# Revit family: Casement_34_E_Side_Hung_Standard
name_source: partatom
category: Windows
revit_build: Autodesk Revit 2014 (Build: 20130308_1515(x64)
units: mm (PartAtom-declared; Revit-internal decimal feet)

## types (17) — shared parameters
Aluminium Thickness = 1 mm  [stored 0.00328084 ft]
Area Pane Left Top = 0.52 m²
Bead SG Gap = 13 mm  [stored 0.0426509 ft]
Casement Dimension = 34 mm  [stored 0.111549 ft]
Custom Sash Height = 1154 mm  [stored 3.78609 ft]
Custom Sash Width = 554 mm  [stored 1.81759 ft]
DG Extrusion Start = 7 mm  [stored 0.0229659 ft]
DG Gasket Finish = Double Glazing Gasket Material
DG Thickness Calc = 4 mm  [stored 0.0131234 ft]
Default Sill Height = 800 mm  [stored 2.62467 ft]
Depth Bead = 20 mm  [stored 0.0656168 ft]
Description = Window 34mm, Type E side hung
Frame Center Offset = 17 mm
Height Panel 1 = 1139 mm  [stored 3.73688 ft]
Height Sash = 1124 mm  [stored 3.68766 ft]
Height Sash Opening = 1154 mm  [stored 3.78609 ft]
Length Transom = 540 mm  [stored 1.77165 ft]
Limit Fixed Pane Height Max = 1800 mm
Limit Fixed Pane Height Min = 200 mm  [stored 0.656168 ft]
Limit Fixed Pane Width Max = 1500 mm  [stored 4.92126 ft]
Limit Fixed Pane Width Min = 200 mm  [stored 0.656168 ft]
Limit Sash Height Max = 1500 mm  [stored 4.92126 ft]
Limit Sash Height Min = 300 mm  [stored 0.984252 ft]
Limit Sash Width Max = 700 mm  [stored 2.29659 ft]
Limit Sash Width Min = 300 mm  [stored 0.984252 ft]
Limit Window Height Max = 1860 mm
Limit Window Height Min = 1430 mm  [stored 4.6916 ft]
Limit Window Width Max = 2130 mm
Limit Window Width Min = 830 mm  [stored 2.7231 ft]
Manufacturer = Crealco
Max System DG One Piece Thickness = 4 mm  [stored 0.0131234 ft]
Max System DG Unit Thickness = 20 mm  [stored 0.0656168 ft]
Model = Casement 34
Offset Bead SG Center Reversed = 17 mm
Offset Mullion Left = 570 mm  [stored 1.87008 ft]
Offset Panel 3 Bead Top = 1200 mm
Offset Panel 4 Left = 600 mm  [stored 1.9685 ft]
Offset Sash Left = 23 mm  [stored 0.0754593 ft]
Offset Sash Top = 23 mm  [stored 0.0754593 ft]
Offset Transom Top = 1170 mm
Offset Window Exterior = 17 mm
SG Gasket Thickness = 6 mm  [stored 0.019685 ft]
Sash Center Offset = 14 mm  [stored 0.0459318 ft]
Sash Overlap = 7 mm  [stored 0.0229659 ft]
Sash Spacing Inner = 8 mm  [stored 0.0262467 ft]
Wall Closure = By host
Width Bead = 15 mm  [stored 0.0492126 ft]
Width Fixed Pane Bottom LHS = 540 mm  [stored 1.77165 ft]
Width Panel 1 = 540 mm  [stored 1.77165 ft]
Width Profile = 30 mm  [stored 0.0984252 ft]
Width Sash = 524 mm  [stored 1.71916 ft]
Width Sash Opening = 554 mm  [stored 1.81759 ft]
zero-valued in all types: Window Exterior Offset

## per-type parameters (varying)
- 34-0915S-1000Pa: Area Pane Left Bottom=0.13 m²; Area Pane Right=0.36 m²; Clearvue Insulated LowE SHGC Value=0.517; Clearvue Insulated LowE U Value=4.01; Clearvue Insulated SHGC Value=0.586; Clearvue Insulated U Value=4.37; Clearvue SHGC Value=0.636; Custom Windload=1000 mm  [stored 3.28084 ft]; Custom Window Height=1490 mm  [stored 4.88845 ft]; Custom Window Width=890 mm  [stored 2.91995 ft]; Depth Mullion=54 mm  [stored 0.177165 ft]; Energy Advantage SHGC Value=0.571; Energy Advantage U Value=5.2; Height=1490 mm  [stored 4.88845 ft]; Height Fixed Pane Bottom LHS=260 mm  [stored 0.853018 ft]; Height Fixed Pane RHS=1430 mm  [stored 4.6916 ft]; Intruderprufe LowE SHGC Value=0.537; Intruderprufe LowE U Value=5.04; Intruderprufe SHGC Value=0.599; Intruderprufe U Value=6.35; Length Mullion=1490 mm  [stored 4.88845 ft]; Max Pane Area=0.52 m²; Mullion Depth Windload Based=54 mm  [stored 0.177165 ft]; Width=890 mm  [stored 2.91995 ft]; Width Fixed Pane RHS=260 mm  [stored 0.853018 ft]; Windload Design=1000 mm  [stored 3.28084 ft]
- 34-0915S-1500Pa: Area Pane Left Bottom=0.13 m²; Area Pane Right=0.36 m²; Clearvue Insulated LowE SHGC Value=0.517; Clearvue Insulated LowE U Value=4.01; Clearvue Insulated SHGC Value=0.586; Clearvue Insulated U Value=4.37; Clearvue SHGC Value=0.636; Custom Windload=1500 mm  [stored 4.92126 ft]; Custom Window Height=1490 mm  [stored 4.88845 ft]; Custom Window Width=890 mm  [stored 2.91995 ft]; Depth Mullion=54 mm  [stored 0.177165 ft]; Energy Advantage SHGC Value=0.571; Energy Advantage U Value=5.2; Height=1490 mm  [stored 4.88845 ft]; Height Fixed Pane Bottom LHS=260 mm  [stored 0.853018 ft]; Height Fixed Pane RHS=1430 mm  [stored 4.6916 ft]; Intruderprufe LowE SHGC Value=0.537; Intruderprufe LowE U Value=5.04; Intruderprufe SHGC Value=0.599; Intruderprufe U Value=6.35; Length Mullion=1490 mm  [stored 4.88845 ft]; Max Pane Area=0.52 m²; Mullion Depth Windload Based=54 mm  [stored 0.177165 ft]; Width=890 mm  [stored 2.91995 ft]; Width Fixed Pane RHS=260 mm  [stored 0.853018 ft]; Windload Design=1500 mm  [stored 4.92126 ft]
- 34-0915S-2000Pa: Area Pane Left Bottom=0.13 m²; Area Pane Right=0.36 m²; Clearvue Insulated LowE SHGC Value=0.517; Clearvue Insulated LowE U Value=4.01; Clearvue Insulated SHGC Value=0.586; Clearvue Insulated U Value=4.37; Clearvue SHGC Value=0.636; Custom Windload=2000 mm; Custom Window Height=1490 mm  [stored 4.88845 ft]; Custom Window Width=890 mm  [stored 2.91995 ft]; Depth Mullion=54 mm  [stored 0.177165 ft]; Energy Advantage SHGC Value=0.571; Energy Advantage U Value=5.2; Height=1490 mm  [stored 4.88845 ft]; Height Fixed Pane Bottom LHS=260 mm  [stored 0.853018 ft]; Height Fixed Pane RHS=1430 mm  [stored 4.6916 ft]; Intruderprufe LowE SHGC Value=0.537; Intruderprufe LowE U Value=5.04; Intruderprufe SHGC Value=0.599; Intruderprufe U Value=6.35; Length Mullion=1490 mm  [stored 4.88845 ft]; Max Pane Area=0.52 m²; Mullion Depth Windload Based=54 mm  [stored 0.177165 ft]; Width=890 mm  [stored 2.91995 ft]; Width Fixed Pane RHS=260 mm  [stored 0.853018 ft]; Windload Design=2000 mm
- 34-1515S-1000Pa: Area Pane Left Bottom=0.13 m²; Area Pane Right=1.21 m²; Clearvue Insulated LowE SHGC Value=0.621; Clearvue Insulated LowE U Value=3.57; Clearvue Insulated SHGC Value=0.694; Clearvue Insulated U Value=4.15; Clearvue SHGC Value=0.769; Custom Windload=1000 mm  [stored 3.28084 ft]; Custom Window Height=1490 mm  [stored 4.88845 ft]; Custom Window Width=1490 mm  [stored 4.88845 ft]; Depth Mullion=54 mm  [stored 0.177165 ft]; Energy Advantage SHGC Value=0.689; Energy Advantage U Value=5.08; Height=1490 mm  [stored 4.88845 ft]; Height Fixed Pane Bottom LHS=260 mm  [stored 0.853018 ft]; Height Fixed Pane RHS=1430 mm  [stored 4.6916 ft]; Intruderprufe LowE SHGC Value=0.644; Intruderprufe LowE U Value=4.9; Intruderprufe SHGC Value=0.726; Intruderprufe U Value=6.68; Length Mullion=1490 mm  [stored 4.88845 ft]; Max Pane Area=1.21 m²; Mullion Depth Windload Based=54 mm  [stored 0.177165 ft]; Width=1490 mm  [stored 4.88845 ft]; Width Fixed Pane RHS=860 mm  [stored 2.82152 ft]; Windload Design=1000 mm  [stored 3.28084 ft]
- 34-1515S-1500Pa: Area Pane Left Bottom=0.13 m²; Area Pane Right=1.21 m²; Clearvue Insulated LowE SHGC Value=0.621; Clearvue Insulated LowE U Value=3.57; Clearvue Insulated SHGC Value=0.694; Clearvue Insulated U Value=4.15; Clearvue SHGC Value=0.769; Custom Windload=1500 mm  [stored 4.92126 ft]; Custom Window Height=1490 mm  [stored 4.88845 ft]; Custom Window Width=1490 mm  [stored 4.88845 ft]; Depth Mullion=54 mm  [stored 0.177165 ft]; Energy Advantage SHGC Value=0.689; Energy Advantage U Value=5.08; Height=1490 mm  [stored 4.88845 ft]; Height Fixed Pane Bottom LHS=260 mm  [stored 0.853018 ft]; Height Fixed Pane RHS=1430 mm  [stored 4.6916 ft]; Intruderprufe LowE SHGC Value=0.644; Intruderprufe LowE U Value=4.9; Intruderprufe SHGC Value=0.726; Intruderprufe U Value=6.68; Length Mullion=1490 mm  [stored 4.88845 ft]; Max Pane Area=1.21 m²; Mullion Depth Windload Based=54 mm  [stored 0.177165 ft]; Width=1490 mm  [stored 4.88845 ft]; Width Fixed Pane RHS=860 mm  [stored 2.82152 ft]; Windload Design=1500 mm  [stored 4.92126 ft]
- 34-1515S-2000Pa: Area Pane Left Bottom=0.13 m²; Area Pane Right=1.21 m²; Clearvue Insulated LowE SHGC Value=0.623; Clearvue Insulated LowE U Value=3.61; Clearvue Insulated SHGC Value=0.684; Clearvue Insulated U Value=4.27; Clearvue SHGC Value=0.77; Custom Windload=2000 mm; Custom Window Height=1490 mm  [stored 4.88845 ft]; Custom Window Width=1490 mm  [stored 4.88845 ft]; Depth Mullion=70 mm  [stored 0.229659 ft]; Energy Advantage SHGC Value=0.689; Energy Advantage U Value=5.16; Height=1490 mm  [stored 4.88845 ft]; Height Fixed Pane Bottom LHS=260 mm  [stored 0.853018 ft]; Height Fixed Pane RHS=1430 mm  [stored 4.6916 ft]; Intruderprufe LowE SHGC Value=0.644; Intruderprufe LowE U Value=4.95; Intruderprufe SHGC Value=0.727; Intruderprufe U Value=6.85; Length Mullion=1490 mm  [stored 4.88845 ft]; Max Pane Area=1.21 m²; Mullion Depth Windload Based=70 mm  [stored 0.229659 ft]; Width=1490 mm  [stored 4.88845 ft]; Width Fixed Pane RHS=860 mm  [stored 2.82152 ft]; Windload Design=2000 mm
- 34-0918S-1000Pa: Area Pane Left Bottom=0.29 m²; Area Pane Right=0.43 m²; Clearvue Insulated LowE SHGC Value=0.556; Clearvue Insulated LowE U Value=4.1; Clearvue Insulated SHGC Value=0.629; Clearvue Insulated U Value=4.51; Clearvue SHGC Value=0.685; Custom Windload=1000 mm  [stored 3.28084 ft]; Custom Window Height=1790 mm; Custom Window Width=890 mm  [stored 2.91995 ft]; Depth Mullion=54 mm  [stored 0.177165 ft]; Energy Advantage SHGC Value=0.615; Energy Advantage U Value=5.39; Height=1790 mm; Height Fixed Pane Bottom LHS=560 mm; Height Fixed Pane RHS=1730 mm; Intruderprufe LowE SHGC Value=0.577; Intruderprufe LowE U Value=5.23; Intruderprufe SHGC Value=0.646; Intruderprufe U Value=6.65; Length Mullion=1790 mm; Max Pane Area=0.52 m²; Mullion Depth Windload Based=54 mm  [stored 0.177165 ft]; Width=890 mm  [stored 2.91995 ft]; Width Fixed Pane RHS=260 mm  [stored 0.853018 ft]; Windload Design=1000 mm  [stored 3.28084 ft]
- 34-0918S-1500Pa: Area Pane Left Bottom=0.29 m²; Area Pane Right=0.43 m²; Clearvue Insulated LowE SHGC Value=0.556; Clearvue Insulated LowE U Value=4.1; Clearvue Insulated SHGC Value=0.629; Clearvue Insulated U Value=4.51; Clearvue SHGC Value=0.685; Custom Windload=1500 mm  [stored 4.92126 ft]; Custom Window Height=1790 mm; Custom Window Width=890 mm  [stored 2.91995 ft]; Depth Mullion=54 mm  [stored 0.177165 ft]; Energy Advantage SHGC Value=0.615; Energy Advantage U Value=5.39; Height=1790 mm; Height Fixed Pane Bottom LHS=560 mm; Height Fixed Pane RHS=1730 mm; Intruderprufe LowE SHGC Value=0.577; Intruderprufe LowE U Value=5.23; Intruderprufe SHGC Value=0.646; Intruderprufe U Value=6.65; Length Mullion=1790 mm; Max Pane Area=0.52 m²; Mullion Depth Windload Based=54 mm  [stored 0.177165 ft]; Width=890 mm  [stored 2.91995 ft]; Width Fixed Pane RHS=260 mm  [stored 0.853018 ft]; Windload Design=1500 mm  [stored 4.92126 ft]
- 34-0918S-2000Pa: Area Pane Left Bottom=0.29 m²; Area Pane Right=0.43 m²; Clearvue Insulated LowE SHGC Value=0.559; Clearvue Insulated LowE U Value=4.1; Clearvue Insulated SHGC Value=0.613; Clearvue Insulated U Value=4.7; Clearvue SHGC Value=0.686; Custom Windload=2000 mm; Custom Window Height=1790 mm; Custom Window Width=890 mm  [stored 2.91995 ft]; Depth Mullion=70 mm  [stored 0.229659 ft]; Energy Advantage SHGC Value=0.615; Energy Advantage U Value=5.5; Height=1790 mm; Height Fixed Pane Bottom LHS=560 mm; Height Fixed Pane RHS=1730 mm; Intruderprufe LowE SHGC Value=0.578; Intruderprufe LowE U Value=5.32; Intruderprufe SHGC Value=0.647; Intruderprufe U Value=6.93; Length Mullion=1790 mm; Max Pane Area=0.52 m²; Mullion Depth Windload Based=70 mm  [stored 0.229659 ft]; Width=890 mm  [stored 2.91995 ft]; Width Fixed Pane RHS=260 mm  [stored 0.853018 ft]; Windload Design=2000 mm
- 34-1218S-1000Pa: Area Pane Left Bottom=0.29 m²; Area Pane Right=0.95 m²; Clearvue Insulated LowE SHGC Value=0.64; Clearvue Insulated LowE U Value=3.94; Clearvue Insulated SHGC Value=0.718; Clearvue Insulated U Value=4.5; Clearvue SHGC Value=0.791; Custom Windload=1000 mm  [stored 3.28084 ft]; Custom Window Height=1790 mm; Custom Window Width=1190 mm  [stored 3.9042 ft]; Depth Mullion=54 mm  [stored 0.177165 ft]; Energy Advantage SHGC Value=0.709; Energy Advantage U Value=5.47; Height=1790 mm; Height Fixed Pane Bottom LHS=560 mm; Height Fixed Pane RHS=1730 mm; Intruderprufe LowE SHGC Value=0.664; Intruderprufe LowE U Value=5.3; Intruderprufe SHGC Value=0.747; Intruderprufe U Value=7.06; Length Mullion=1790 mm; Max Pane Area=0.95 m²; Mullion Depth Windload Based=54 mm  [stored 0.177165 ft]; Width=1190 mm  [stored 3.9042 ft]; Width Fixed Pane RHS=560 mm; Windload Design=1000 mm  [stored 3.28084 ft]
- 34-1218S-1500Pa: Area Pane Left Bottom=0.29 m²; Area Pane Right=0.95 m²; Clearvue Insulated LowE SHGC Value=0.642; Clearvue Insulated LowE U Value=3.99; Clearvue Insulated SHGC Value=0.705; Clearvue Insulated U Value=4.65; Clearvue SHGC Value=0.792; Custom Windload=1500 mm  [stored 4.92126 ft]; Custom Window Height=1790 mm; Custom Window Width=1190 mm  [stored 3.9042 ft]; Depth Mullion=70 mm  [stored 0.229659 ft]; Energy Advantage SHGC Value=0.709; Energy Advantage U Value=5.56; Height=1790 mm; Height Fixed Pane Bottom LHS=560 mm; Height Fixed Pane RHS=1730 mm; Intruderprufe LowE SHGC Value=0.664; Intruderprufe LowE U Value=5.37; Intruderprufe SHGC Value=0.748; Intruderprufe U Value=7.28; Length Mullion=1790 mm; Max Pane Area=0.95 m²; Mullion Depth Windload Based=70 mm  [stored 0.229659 ft]; Width=1190 mm  [stored 3.9042 ft]; Width Fixed Pane RHS=560 mm; Windload Design=1500 mm  [stored 4.92126 ft]
- 34-1218S-2000Pa: Area Pane Left Bottom=0.29 m²; Area Pane Right=0.95 m²; Clearvue Insulated LowE SHGC Value=0.642; Clearvue Insulated LowE U Value=3.99; Clearvue Insulated SHGC Value=0.705; Clearvue Insulated U Value=4.65; Clearvue SHGC Value=0.792; Custom Windload=2000 mm; Custom Window Height=1790 mm; Custom Window Width=1190 mm  [stored 3.9042 ft]; Depth Mullion=70 mm  [stored 0.229659 ft]; Energy Advantage SHGC Value=0.709; Energy Advantage U Value=5.56; Height=1790 mm; Height Fixed Pane Bottom LHS=560 mm; Height Fixed Pane RHS=1730 mm; Intruderprufe LowE SHGC Value=0.664; Intruderprufe LowE U Value=5.37; Intruderprufe SHGC Value=0.748; Intruderprufe U Value=7.28; Length Mullion=1790 mm; Max Pane Area=0.95 m²; Mullion Depth Windload Based=70 mm  [stored 0.229659 ft]; Width=1190 mm  [stored 3.9042 ft]; Width Fixed Pane RHS=560 mm; Windload Design=2000 mm
- 34-1518S-1000Pa: Area Pane Left Bottom=0.29 m²; Area Pane Right=1.46 m²; Clearvue Insulated LowE SHGC Value=0.696; Clearvue Insulated LowE U Value=3.83; Clearvue Insulated SHGC Value=0.777; Clearvue Insulated U Value=4.49; Clearvue SHGC Value=0; Custom Windload=1000 mm  [stored 3.28084 ft]; Custom Window Height=1790 mm; Custom Window Width=1490 mm  [stored 4.88845 ft]; Depth Mullion=54 mm  [stored 0.177165 ft]; Energy Advantage SHGC Value=0; Energy Advantage U Value=7.9; Height=1790 mm; Height Fixed Pane Bottom LHS=560 mm; Height Fixed Pane RHS=1730 mm; Intruderprufe LowE SHGC Value=0.722; Intruderprufe LowE U Value=5.34; Intruderprufe SHGC Value=0.814; Intruderprufe U Value=7.34; Length Mullion=1790 mm; Max Pane Area=1.46 m²; Mullion Depth Windload Based=54 mm  [stored 0.177165 ft]; Width=1490 mm  [stored 4.88845 ft]; Width Fixed Pane RHS=860 mm  [stored 2.82152 ft]; Windload Design=1000 mm  [stored 3.28084 ft]
- 34-1518S-1500Pa: Area Pane Left Bottom=0.29 m²; Area Pane Right=1.46 m²; Clearvue Insulated LowE SHGC Value=0.697; Clearvue Insulated LowE U Value=3.87; Clearvue Insulated SHGC Value=0.766; Clearvue Insulated U Value=4.61; Clearvue SHGC Value=0; Custom Windload=1500 mm  [stored 4.92126 ft]; Custom Window Height=1790 mm; Custom Window Width=1490 mm  [stored 4.88845 ft]; Depth Mullion=70 mm  [stored 0.229659 ft]; Energy Advantage SHGC Value=0; Energy Advantage U Value=7.9; Height=1790 mm; Height Fixed Pane Bottom LHS=560 mm; Height Fixed Pane RHS=1730 mm; Intruderprufe LowE SHGC Value=0.722; Intruderprufe LowE U Value=5.4; Intruderprufe SHGC Value=0.816; Intruderprufe U Value=7.52; Length Mullion=1790 mm; Max Pane Area=1.46 m²; Mullion Depth Windload Based=70 mm  [stored 0.229659 ft]; URL=http://www.crealco.co.za; Width=1490 mm  [stored 4.88845 ft]; Width Fixed Pane RHS=860 mm  [stored 2.82152 ft]; Windload Design=1500 mm  [stored 4.92126 ft]
- 34-1215S-1000Pa: Area Pane Left Bottom=0.13 m²; Area Pane Right=0.78 m²; Clearvue Insulated LowE SHGC Value=0.581; Clearvue Insulated LowE U Value=3.74; Clearvue Insulated SHGC Value=0.652; Clearvue Insulated U Value=4.23; Clearvue SHGC Value=0.718; Custom Windload=1000 mm  [stored 3.28084 ft]; Custom Window Height=1490 mm  [stored 4.88845 ft]; Custom Window Width=1190 mm  [stored 3.9042 ft]; Depth Mullion=54 mm  [stored 0.177165 ft]; Energy Advantage SHGC Value=0.643; Energy Advantage U Value=5.13; Height=1490 mm  [stored 4.88845 ft]; Height Fixed Pane Bottom LHS=260 mm  [stored 0.853018 ft]; Height Fixed Pane RHS=1430 mm  [stored 4.6916 ft]; Intruderprufe LowE SHGC Value=0.603; Intruderprufe LowE U Value=4.65; Intruderprufe SHGC Value=0.677; Intruderprufe U Value=6.55; Length Mullion=1490 mm  [stored 4.88845 ft]; Max Pane Area=0.78 m²; Mullion Depth Windload Based=54 mm  [stored 0.177165 ft]; Width=1190 mm  [stored 3.9042 ft]; Width Fixed Pane RHS=560 mm; Windload Design=1000 mm  [stored 3.28084 ft]
- 34-1215S-1500Pa: Area Pane Left Bottom=0.13 m²; Area Pane Right=0.78 m²; Clearvue Insulated LowE SHGC Value=0.581; Clearvue Insulated LowE U Value=3.74; Clearvue Insulated SHGC Value=0.652; Clearvue Insulated U Value=4.23; Clearvue SHGC Value=0.718; Custom Windload=1500 mm  [stored 4.92126 ft]; Custom Window Height=1490 mm  [stored 4.88845 ft]; Custom Window Width=1190 mm  [stored 3.9042 ft]; Depth Mullion=54 mm  [stored 0.177165 ft]; Energy Advantage SHGC Value=0.643; Energy Advantage U Value=5.13; Height=1490 mm  [stored 4.88845 ft]; Height Fixed Pane Bottom LHS=260 mm  [stored 0.853018 ft]; Height Fixed Pane RHS=1430 mm  [stored 4.6916 ft]; Intruderprufe LowE SHGC Value=0.603; Intruderprufe LowE U Value=4.65; Intruderprufe SHGC Value=0.677; Intruderprufe U Value=6.55; Length Mullion=1490 mm  [stored 4.88845 ft]; Max Pane Area=0.78 m²; Mullion Depth Windload Based=54 mm  [stored 0.177165 ft]; Width=1190 mm  [stored 3.9042 ft]; Width Fixed Pane RHS=560 mm; Windload Design=1500 mm  [stored 4.92126 ft]
- 34-1215S-2000Pa: Area Pane Left Bottom=0.13 m²; Area Pane Right=0.78 m²; Clearvue Insulated LowE SHGC Value=0.581; Clearvue Insulated LowE U Value=3.74; Clearvue Insulated SHGC Value=0.652; Clearvue Insulated U Value=4.23; Clearvue SHGC Value=0.718; Custom Windload=2000 mm; Custom Window Height=1490 mm  [stored 4.88845 ft]; Custom Window Width=1190 mm  [stored 3.9042 ft]; Depth Mullion=54 mm  [stored 0.177165 ft]; Energy Advantage SHGC Value=0.643; Energy Advantage U Value=5.13; Height=1490 mm  [stored 4.88845 ft]; Height Fixed Pane Bottom LHS=260 mm  [stored 0.853018 ft]; Height Fixed Pane RHS=1430 mm  [stored 4.6916 ft]; Intruderprufe LowE SHGC Value=0.603; Intruderprufe LowE U Value=4.65; Intruderprufe SHGC Value=0.677; Intruderprufe U Value=6.55; Length Mullion=1490 mm  [stored 4.88845 ft]; Max Pane Area=0.78 m²; Mullion Depth Windload Based=54 mm  [stored 0.177165 ft]; Width=1190 mm  [stored 3.9042 ft]; Width Fixed Pane RHS=560 mm; Windload Design=2000 mm

note: [stored X ft] marks values corroborated as IEEE doubles in the binary element streams (Revit-internal decimal feet)

## geometry (parser evidence)
native form markers: Blend x4, Extrusion x1, Sweep x28
no freeform markers — native parametric forms only
